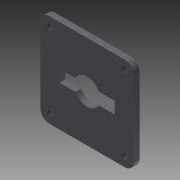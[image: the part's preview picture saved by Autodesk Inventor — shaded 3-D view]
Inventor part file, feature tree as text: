
AUTODESK INVENTOR PART (.ipt)
format: ipt  version: 2012 (Build 160160000, 160)  size: 196,608 bytes
history: native  units: in
note: dims shown in document units (in); Inventor stores cm internally (conversion verified against a paired STEP export)
features: extrude x5, fillet x3, sketch x1, hole x1
ambient origin geometry x8: Origin, YZ Plane, XZ Plane, XY Plane, X Axis, Y Axis, Z Axis, Center Point
bodies: Solid1 (feature_tree)
feature tree (10):
  sketch  "Sketch1"  dims[d0=0.9449in d1=0.4724in d2=1.0236in d3=0.5118in d4=0.0787in d5=0.2559in d6=0.128in d7=0.0787in d8=0.5625in d9=2.0in d10=1.0in d11=2.0in d12=1.0in d13=0.1181in d14=0.3937in d15=0.1575in d16=0.1575in d17=0.1575in d18=0.1575in d19=0.1575in d20=0.2in d21=0.2in d22=0.2in d23=0.2in d24=0.125in d25=0.0in d26=0.125in d34=1.6in d35=1.6in d44=0.25in d45=0.125in d46=0.0in d47=0.125in d48=0.0in d49=0.125in d50=0.0in d51=0.125in d52=0.0in d53=0.13in d54=0.75in d55=0.375in d56=0.25in d57=0.5635in d58=1.0in d59=0.8108in d60=0.1875in]
  extrude  "Extrusion1"  Depth=0.4724in
  fillet  "Fillet1"  Radius=1.0236in
  fillet  "Fillet2"  Radius=0.5118in
  extrude  "Extrusion2"  Depth=0.0787in
  extrude  "Extrusion3"  Depth=0.2559in
  extrude  "Extrusion4"  Depth=0.128in
  extrude  "Extrusion5"  Depth=0.0787in
  hole  "Hole2"  [1 undecoded]
  fillet  "Fillet3"  Radius=2.0in
note: 1 required parameter value undecoded (feature->parameter linkage not recoverable at this tier; creation-order binding heuristic only, values carry confidence <= 0.55)
